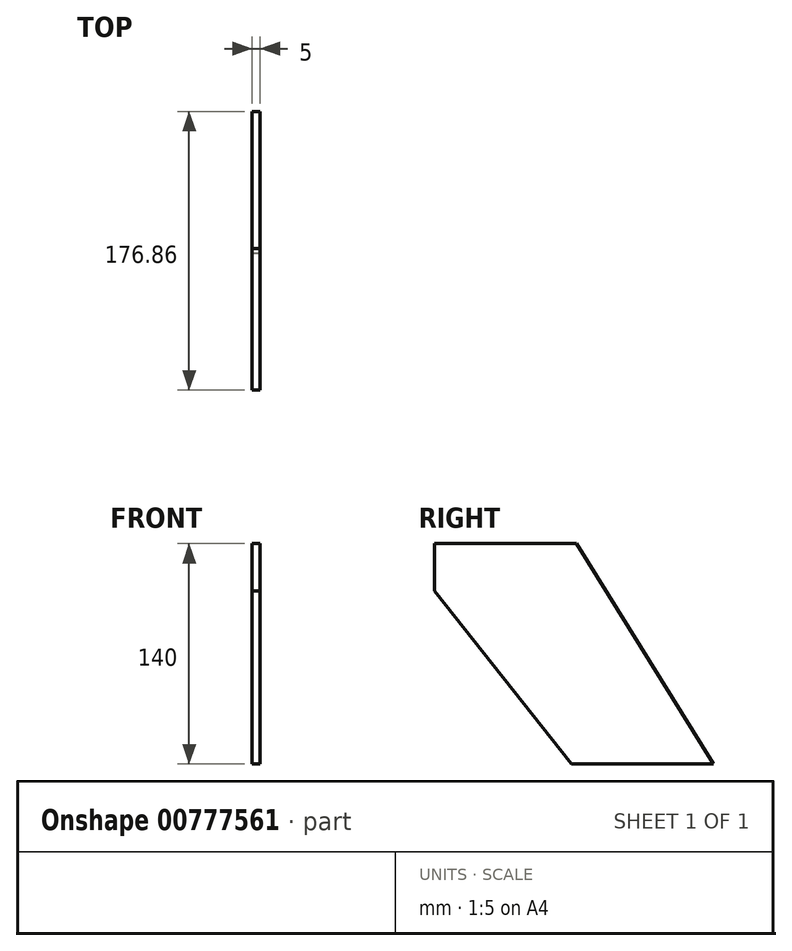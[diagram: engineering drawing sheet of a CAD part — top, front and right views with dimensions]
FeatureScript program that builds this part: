
annotation { "Feature Type Name" : "Feature", "Feature Type Description" : "" }
export const myFeature = defineFeature(function(context is Context, id is Id, definition is map)
    precondition{}
    {
        {
            var Q0;
            Q0=qCreatedBy(makeId("Right.planeOp"), FACE);
            var sketch = newSketch(context, id + "F0", { "sketchPlane" : qUnion([Q0])});
            skLineSegment(sketch, "E0", {"start": v(0, 0) * mm, "end": v(-90, 0) * mm});
            skLineSegment(sketch, "E1", {"start": v(-176.86, 110) * mm, "end": v(-176.86, 140) * mm});
            skLineSegment(sketch, "E2", {"start": v(-176.86, 140) * mm, "end": v(-86.86, 140) * mm});
            skLineSegment(sketch, "E3", {"start": v(-86.86, 140) * mm, "end": v(0, 0) * mm});
            skPoint(sketch, "E4.visualSharp", {"position": v(-86.86, 140) * mm});
            skLineSegment(sketch, "E5", {"start": v(-176.86, 110) * mm, "end": v(-90, 0) * mm});
            skSolve(sketch);
        }
        {
            var Q0;
            Q0 = qSketchRegion(id + "F0", true);
            extrude(context, id + "F1", {"entities" : qUnion([Q0]), "flatOperationType" : FlatOperationType.REMOVE, "depth" : 5 * mm, "offsetDistance" : 25 * mm, "domain" : OperationDomain.MODEL});
        }
    });
